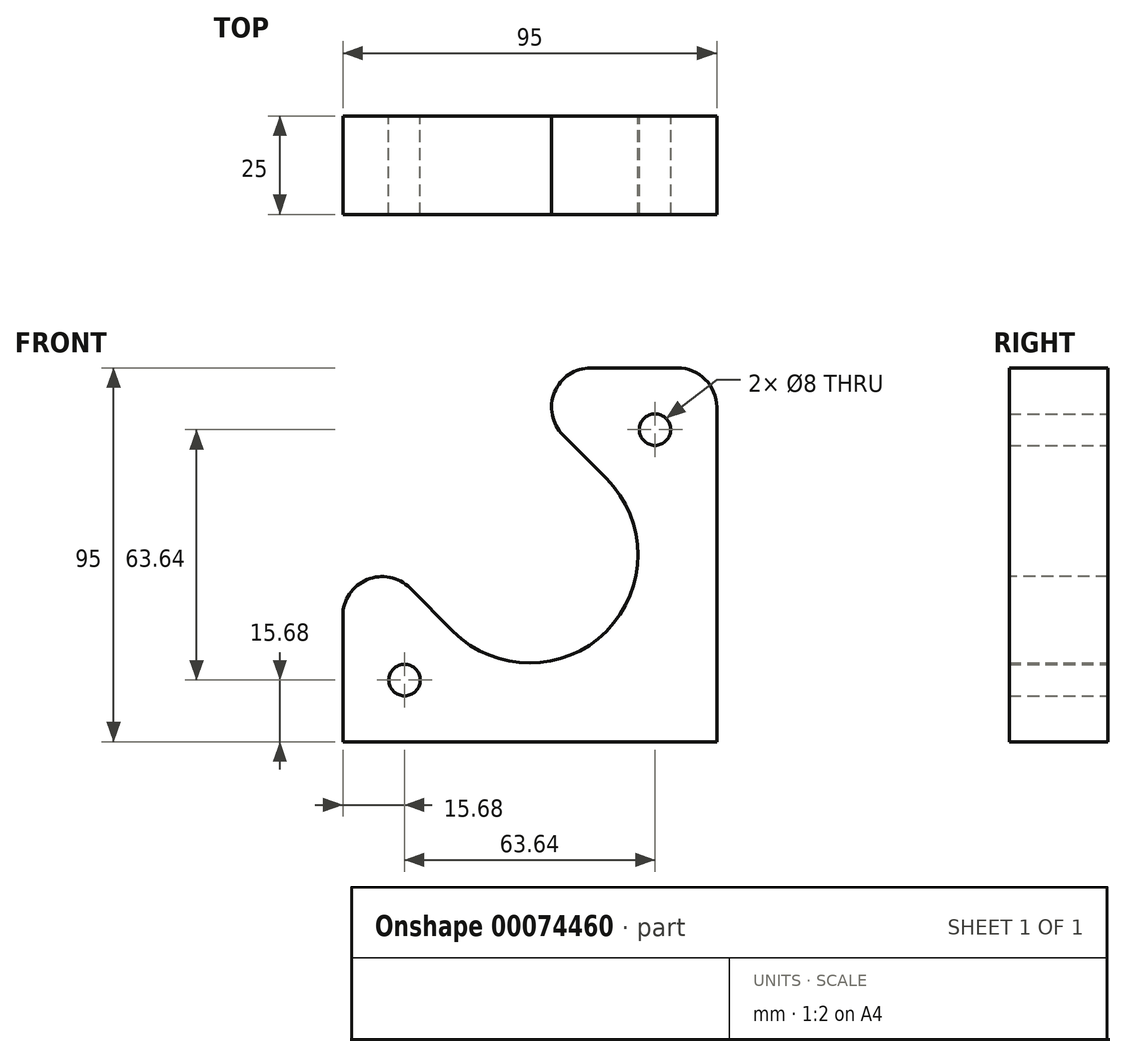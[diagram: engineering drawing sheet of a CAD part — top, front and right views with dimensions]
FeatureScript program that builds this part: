
annotation { "Feature Type Name" : "Feature", "Feature Type Description" : "" }
export const myFeature = defineFeature(function(context is Context, id is Id, definition is map)
    precondition{}
    {
        {
            var Q0;
            Q0=qCreatedBy(makeId("Front.planeOp"),FACE);
            var sketch = newSketch(context, id + "F0", { "sketchPlane" : qUnion([Q0])});
            skLineSegment(sketch, "E0.bottom", {"start": v(0, 0) * mm, "end": v(95, 0) * mm});
            skLineSegment(sketch, "E0.top", {"start": v(0, 95) * mm, "end": v(95, 95) * mm});
            skLineSegment(sketch, "E0.left", {"start": v(0, 0) * mm, "end": v(0, 95) * mm});
            skLineSegment(sketch, "E0.right", {"start": v(95, 0) * mm, "end": v(95, 95) * mm});
            skCircle(sketch, "E1", {"center": v(47.5, 47.5) * mm, "radius": 27.5 * mm});
            skCircle(sketch, "E2", {"center": v(79.32, 79.32) * mm, "radius": 4 * mm});
            skCircle(sketch, "E3", {"center": v(15.68, 15.68) * mm, "radius": 4 * mm});
            skLineSegment(sketch, "E4", {"start": v(0, 0) * mm, "end": v(95, 95) * mm, "construction": true});
            skLineSegment(sketch, "E5", {"start": v(66.95, 66.95) * mm, "end": v(38.9, 95) * mm});
            skLineSegment(sketch, "E6", {"start": v(28.05, 28.05) * mm, "end": v(0, 56.1) * mm});
            skSolve(sketch);
        }
        {
            var Q0;
            {var subQ2=sQuery(id+"F0.wireOp",EDGE,"E0.bottom");Q0=makeQuery(id+"F0.imprint","IMPRINT",FACE,{"disambiguationData":[TD([[makeQuery(id+"F0.imprint","IMPRINT",EDGE,{"derivedFrom":subQ2}),1.0]])]});}
            extrude(context, id + "F1", {"entities" : qUnion([Q0]), "depth" : 25 * mm});
        }
        {
            var Q0;
            Q0=makeQuery(id+"F1.opExtrude","SWEPT_EDGE",EDGE,{"disambiguationData":[OSD([sQuery(id+"F0.wireOp",EDGE,"E0.top"),sQuery(id+"F0.wireOp",EDGE,"E0.right")])]});
            var Q1;
            Q1=makeQuery(id+"F1.opExtrude","SWEPT_EDGE",EDGE,{"disambiguationData":[OSD([sQuery(id+"F0.wireOp",EDGE,"E0.top"),sQuery(id+"F0.wireOp",EDGE,"E5")])]});
            var Q2;
            Q2=makeQuery(id+"F1.opExtrude","SWEPT_EDGE",EDGE,{"disambiguationData":[OSD([sQuery(id+"F0.wireOp",EDGE,"E0.left"),sQuery(id+"F0.wireOp",EDGE,"E6")])]});
            fillet(context, id + "F2", {"entities" : qUnion([Q0, Q1, Q2]), "radius" : 10 * mm, "tangentPropagation" : true, "allowEdgeOverflow" : false});
        }
    });
